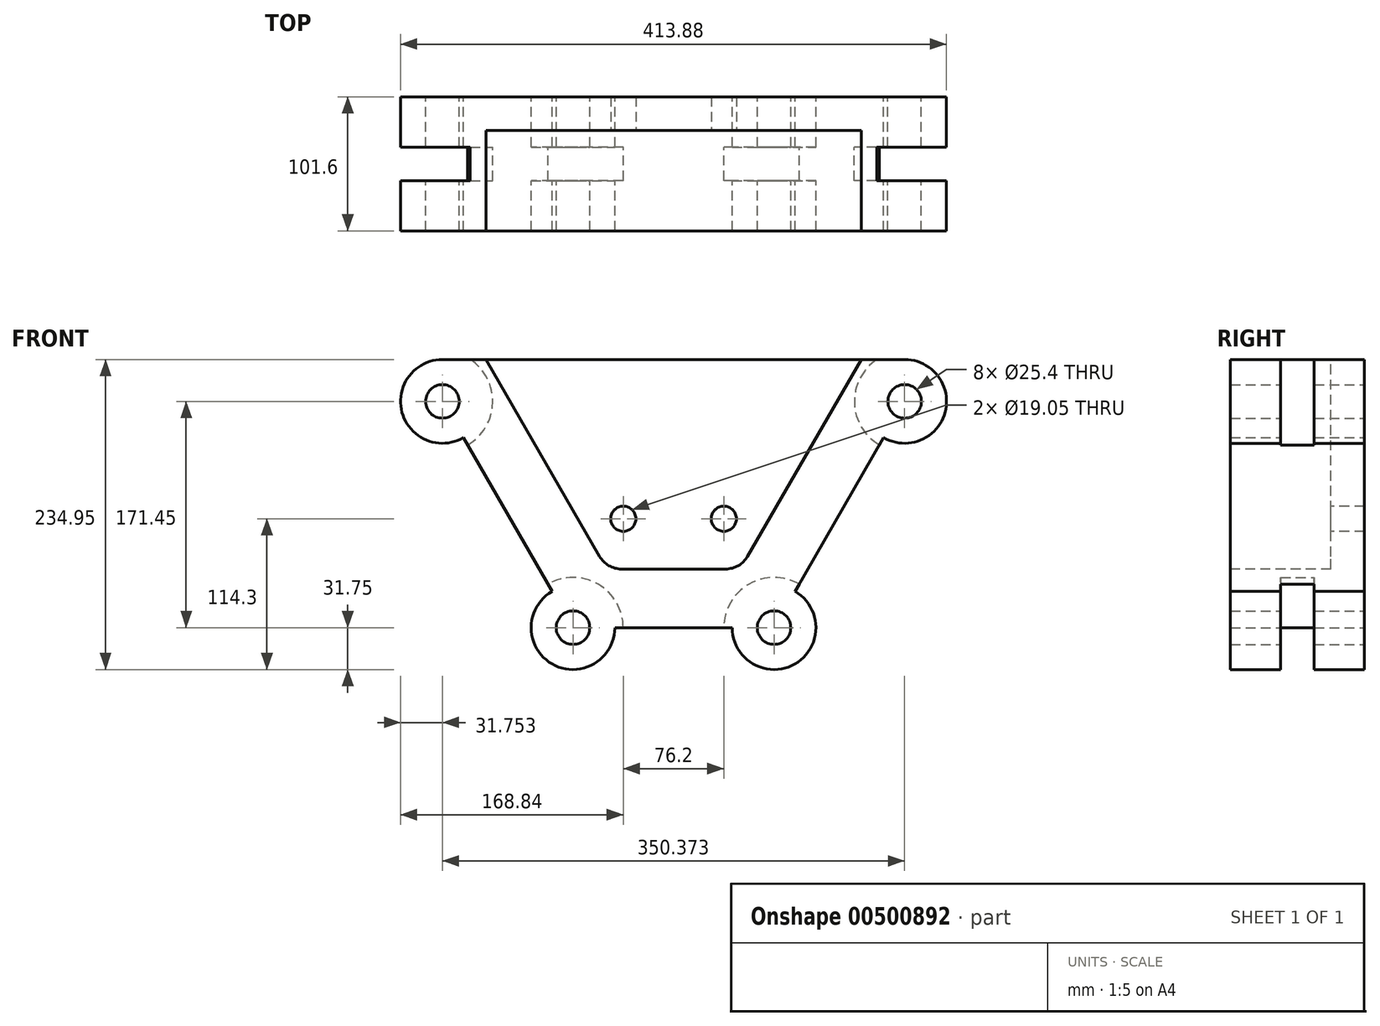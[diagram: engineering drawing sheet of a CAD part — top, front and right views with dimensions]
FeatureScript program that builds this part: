
annotation { "Feature Type Name" : "Feature", "Feature Type Description" : "" }
export const myFeature = defineFeature(function(context is Context, id is Id, definition is map)
    precondition{}
    {
        {
            var Q0;
            Q0=qCreatedBy(makeId("Front.planeOp"),FACE);
            var sketch = newSketch(context, id + "F0", { "sketchPlane" : qUnion([Q0])});
            skLineSegment(sketch, "E0", {"start": v(0, 0) * mm, "end": v(0, 171.45) * mm, "construction": true});
            skLineSegment(sketch, "E1", {"start": v(0, 171.45) * mm, "end": v(175.19, 171.45) * mm, "construction": true});
            skLineSegment(sketch, "E2", {"start": v(175.19, 171.45) * mm, "end": v(76.2, 0) * mm});
            skLineSegment(sketch, "E3", {"start": v(76.2, 0) * mm, "end": v(-76.2, 0) * mm});
            skLineSegment(sketch, "E4", {"start": v(-76.2, 0) * mm, "end": v(-175.19, 171.45) * mm});
            skLineSegment(sketch, "E5", {"start": v(-175.19, 171.45) * mm, "end": v(0, 171.45) * mm, "construction": true});
            skCircle(sketch, "E6", {"center": v(-175.19, 171.45) * mm, "radius": 12.7 * mm});
            skCircle(sketch, "E7", {"center": v(175.19, 171.45) * mm, "radius": 12.7 * mm});
            skCircle(sketch, "E8", {"center": v(76.2, 0) * mm, "radius": 12.7 * mm});
            skCircle(sketch, "E9", {"center": v(-76.2, 0) * mm, "radius": 12.7 * mm});
            skCircle(sketch, "E10", {"center": v(-175.19, 171.45) * mm, "radius": 31.75 * mm});
            skCircle(sketch, "E11", {"center": v(175.19, 171.45) * mm, "radius": 31.75 * mm});
            skCircle(sketch, "E12", {"center": v(76.2, 0) * mm, "radius": 31.75 * mm});
            skCircle(sketch, "E13", {"center": v(-76.2, 0) * mm, "radius": 31.75 * mm});
            skLineSegment(sketch, "E14", {"start": v(-175.19, 203.2) * mm, "end": v(175.19, 203.2) * mm});
            skLineSegment(sketch, "E15", {"start": v(0, 171.45) * mm, "end": v(0, 203.2) * mm, "construction": true});
            skSolve(sketch);
        }
        {
            var Q0;
            Q0=makeQuery(id+"F0.imprint","IMPRINT",FACE,{"disambiguationData":[TD([[makeQuery(id+"F0.imprint","IMPRINT",EDGE,{"derivedFrom":sQuery(id+"F0.wireOp",EDGE,"E6")}),-1.0]])]});
            var Q1;
            {var subQ0=sQuery(id+"F0.wireOp",EDGE,"E14");Q1=makeQuery(id+"F0.imprint","IMPRINT",FACE,{"disambiguationData":[TD([[makeQuery(id+"F0.imprint","IMPRINT",EDGE,{"derivedFrom":subQ0}),-1.0]])]});}
            var Q2;
            Q2=makeQuery(id+"F0.imprint","IMPRINT",FACE,{"disambiguationData":[TD([[makeQuery(id+"F0.imprint","IMPRINT",EDGE,{"derivedFrom":sQuery(id+"F0.wireOp",EDGE,"E7")}),-1.0]])]});
            var Q3;
            {var subQ0=sQuery(id+"F0.wireOp",EDGE,"E12");var subQ1=sQuery(id+"F0.wireOp",EDGE,"E2");var subQ2=makeQuery(id+"F0.imprint","INTERSECT",VERTEX,{"derivedFrom":[subQ1,subQ0]});Q3=makeQuery(id+"F0.imprint","IMPRINT",FACE,{"disambiguationData":[TD([[makeQuery(id+"F0.imprint","IMPRINT",EDGE,{"disambiguationData":[TD([[subQ2,-1.0]])],"derivedFrom":subQ1}),1.0]])]});}
            var Q4;
            {var subQ0=sQuery(id+"F0.wireOp",EDGE,"E12");var subQ1=sQuery(id+"F0.wireOp",EDGE,"E2");var subQ2=makeQuery(id+"F0.imprint","INTERSECT",VERTEX,{"derivedFrom":[subQ1,subQ0]});Q4=makeQuery(id+"F0.imprint","IMPRINT",FACE,{"disambiguationData":[TD([[makeQuery(id+"F0.imprint","IMPRINT",EDGE,{"disambiguationData":[TD([[subQ2,-1.0]])],"derivedFrom":subQ1}),-1.0]])]});}
            var Q5;
            {var subQ0=sQuery(id+"F0.wireOp",EDGE,"E13");var subQ1=sQuery(id+"F0.wireOp",EDGE,"E3");var subQ2=makeQuery(id+"F0.imprint","INTERSECT",VERTEX,{"derivedFrom":[subQ1,subQ0]});Q5=makeQuery(id+"F0.imprint","IMPRINT",FACE,{"disambiguationData":[TD([[makeQuery(id+"F0.imprint","IMPRINT",EDGE,{"disambiguationData":[TD([[subQ2,-1.0]])],"derivedFrom":subQ1}),-1.0]])]});}
            var Q6;
            {var subQ0=sQuery(id+"F0.wireOp",EDGE,"E13");var subQ1=sQuery(id+"F0.wireOp",EDGE,"E3");var subQ2=makeQuery(id+"F0.imprint","INTERSECT",VERTEX,{"derivedFrom":[subQ1,subQ0]});Q6=makeQuery(id+"F0.imprint","IMPRINT",FACE,{"disambiguationData":[TD([[makeQuery(id+"F0.imprint","IMPRINT",EDGE,{"disambiguationData":[TD([[subQ2,-1.0]])],"derivedFrom":subQ1}),1.0]])]});}
            extrude(context, id + "F1", {"entities" : qUnion([Q0, Q1, Q2, Q3, Q4, Q5, Q6]), "endBound" : BoundingType.SYMMETRIC, "depth" : 101.6 * mm});
        }
        {
            var Q0;
            Q0=makeQuery(id+"F1.opExtrude","CAP_FACE",FACE,{"disambiguationData":[OSD([sQuery(id+"F0.wireOp",EDGE,"E2"),sQuery(id+"F0.wireOp",EDGE,"E3"),sQuery(id+"F0.wireOp",EDGE,"E4"),sQuery(id+"F0.wireOp",EDGE,"E6"),sQuery(id+"F0.wireOp",EDGE,"E7"),sQuery(id+"F0.wireOp",EDGE,"E8"),sQuery(id+"F0.wireOp",EDGE,"E9"),sQuery(id+"F0.wireOp",EDGE,"E10"),sQuery(id+"F0.wireOp",EDGE,"E11"),sQuery(id+"F0.wireOp",EDGE,"E12"),sQuery(id+"F0.wireOp",EDGE,"E13"),sQuery(id+"F0.wireOp",EDGE,"E14")])],"isStart":false});
            var sketch = newSketch(context, id + "F2", { "sketchPlane" : qUnion([Q0])});
            skLineSegment(sketch, "E16", {"start": v(0, 0) * mm, "end": v(0, 44.45) * mm, "construction": true});
            skLineSegment(sketch, "E17", {"start": v(0, 44.45) * mm, "end": v(50.54, 44.45) * mm});
            skLineSegment(sketch, "E18", {"start": v(50.54, 44.45) * mm, "end": v(142.2, 203.2) * mm});
            skLineSegment(sketch, "E19", {"start": v(142.2, 203.2) * mm, "end": v(-142.2, 203.2) * mm});
            skLineSegment(sketch, "E20", {"start": v(-142.2, 203.2) * mm, "end": v(-50.54, 44.45) * mm});
            skLineSegment(sketch, "E21", {"start": v(-50.54, 44.45) * mm, "end": v(0, 44.45) * mm});
            skLineSegment(sketch, "E22", {"start": v(-96.36, 123.83) * mm, "end": v(-134.86, 101.6) * mm, "construction": true});
            skSolve(sketch);
        }
        {
            var Q0;
            Q0=makeQuery(id+"F2.imprint","IMPRINT",FACE,{"disambiguationData":[TD([[makeQuery(id+"F2.imprint","IMPRINT",EDGE,{"derivedFrom":sQuery(id+"F2.wireOp",EDGE,"E17")}),1.0]])]});
            extrude(context, id + "F3", {"entities" : qUnion([Q0]), "operationType" : NewBodyOperationType.REMOVE, "oppositeDirection" : true, "depth" : 76.2 * mm});
        }
        {
            var Q0;
            Q0=qCreatedBy(makeId("Front.planeOp"),FACE);
            var sketch = newSketch(context, id + "F4", { "sketchPlane" : qUnion([Q0])});
            skCircle(sketch, "E23", {"center": v(-175.19, 171.45) * mm, "radius": 38.1 * mm});
            skCircle(sketch, "E24", {"center": v(-76.2, 0) * mm, "radius": 38.1 * mm});
            skCircle(sketch, "E25", {"center": v(76.2, 0) * mm, "radius": 38.1 * mm});
            skCircle(sketch, "E26", {"center": v(175.19, 171.45) * mm, "radius": 38.1 * mm});
            skSolve(sketch);
        }
        {
            var Q0;
            Q0 = qSketchRegion(id + "F4", true);
            extrude(context, id + "F5", {"entities" : qUnion([Q0]), "operationType" : NewBodyOperationType.REMOVE, "endBound" : BoundingType.SYMMETRIC, "depth" : 25.4 * mm});
        }
        {
            var Q0;
            Q0=makeQuery(id+"F3.boolean.opBoolean","COPY",FACE,{"derivedFrom":makeQuery(id+"F3.opExtrude","CAP_FACE",FACE,{"disambiguationData":[OSD([sQuery(id+"F2.wireOp",EDGE,"E17"),sQuery(id+"F2.wireOp",EDGE,"E18"),sQuery(id+"F2.wireOp",EDGE,"E19"),sQuery(id+"F2.wireOp",EDGE,"E20"),sQuery(id+"F2.wireOp",EDGE,"E21")])],"isStart":false})});
            var sketch = newSketch(context, id + "F6", { "sketchPlane" : qUnion([Q0])});
            skCircle(sketch, "E27", {"center": v(-38.1, 82.55) * mm, "radius": 9.53 * mm});
            skCircle(sketch, "E28", {"center": v(38.1, 82.55) * mm, "radius": 9.53 * mm});
            skLineSegment(sketch, "E29", {"start": v(-38.1, 82.55) * mm, "end": v(38.1, 82.55) * mm, "construction": true});
            skLineSegment(sketch, "E30", {"start": v(0, 82.55) * mm, "end": v(0, 44.45) * mm, "construction": true});
            skSolve(sketch);
        }
        {
            var Q0;
            Q0=makeQuery(id+"F6.imprint","IMPRINT",FACE,{"disambiguationData":[TD([[makeQuery(id+"F6.imprint","IMPRINT",EDGE,{"derivedFrom":sQuery(id+"F6.wireOp",EDGE,"E28")}),1.0]])]});
            var Q1;
            Q1=makeQuery(id+"F6.imprint","IMPRINT",FACE,{"disambiguationData":[TD([[makeQuery(id+"F6.imprint","IMPRINT",EDGE,{"derivedFrom":sQuery(id+"F6.wireOp",EDGE,"E27")}),1.0]])]});
            extrude(context, id + "F7", {"entities" : qUnion([Q0, Q1]), "operationType" : NewBodyOperationType.REMOVE, "endBound" : BoundingType.THROUGH_ALL, "oppositeDirection" : true, "depth" : 25.4 * mm});
        }
        {
            var Q0;
            Q0=makeQuery(id+"F3.boolean.opBoolean","COPY",EDGE,{"derivedFrom":makeQuery(id+"F3.opExtrude","SWEPT_EDGE",EDGE,{"disambiguationData":[OSD([sQuery(id+"F2.wireOp",EDGE,"E20"),sQuery(id+"F2.wireOp",EDGE,"E21")])]})});
            var Q1;
            Q1=makeQuery(id+"F3.boolean.opBoolean","COPY",EDGE,{"derivedFrom":makeQuery(id+"F3.opExtrude","SWEPT_EDGE",EDGE,{"disambiguationData":[OSD([sQuery(id+"F2.wireOp",EDGE,"E17"),sQuery(id+"F2.wireOp",EDGE,"E18")])]})});
            fillet(context, id + "F8", {"entities" : qUnion([Q0, Q1]), "radius" : 19.05 * mm, "tangentPropagation" : true, "allowEdgeOverflow" : false});
        }
    });
